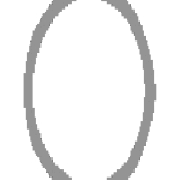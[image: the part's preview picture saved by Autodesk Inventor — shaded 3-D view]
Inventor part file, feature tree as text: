
AUTODESK INVENTOR PART (.ipt)
format: ipt  version: 2021 (Build 250183000, 183)  size: 147,456 bytes
history: native  units: in
note: dims shown in document units (in); Inventor stores cm internally (conversion verified against a paired STEP export)
features: other x5, sketch x2, sweep x1, plane x1
ambient origin geometry x8: Origin, YZ Plane, XZ Plane, XY Plane, X Axis, Y Axis, Z Axis, Center Point
bodies: Solid1 (feature_tree), Body (feature_tree)
feature tree (9):
  other  "Driven Length"
  other  "Frame Generator"
  other  "Start Plane"
  other  "End Plane"
  sweep  "Sweep Path"
  other  "Orientation Work Plane"
  sketch  "Sketch2"  dims[d0=1.0in d1=0.065in]
  plane  "Work Plane3"
  sketch  "Sketch3"  dims[d2=1.1738in d4=-0.0in d5=1.1738in d8=90.0deg d9=1.1738in d10=0.0in d11=0.0in]
